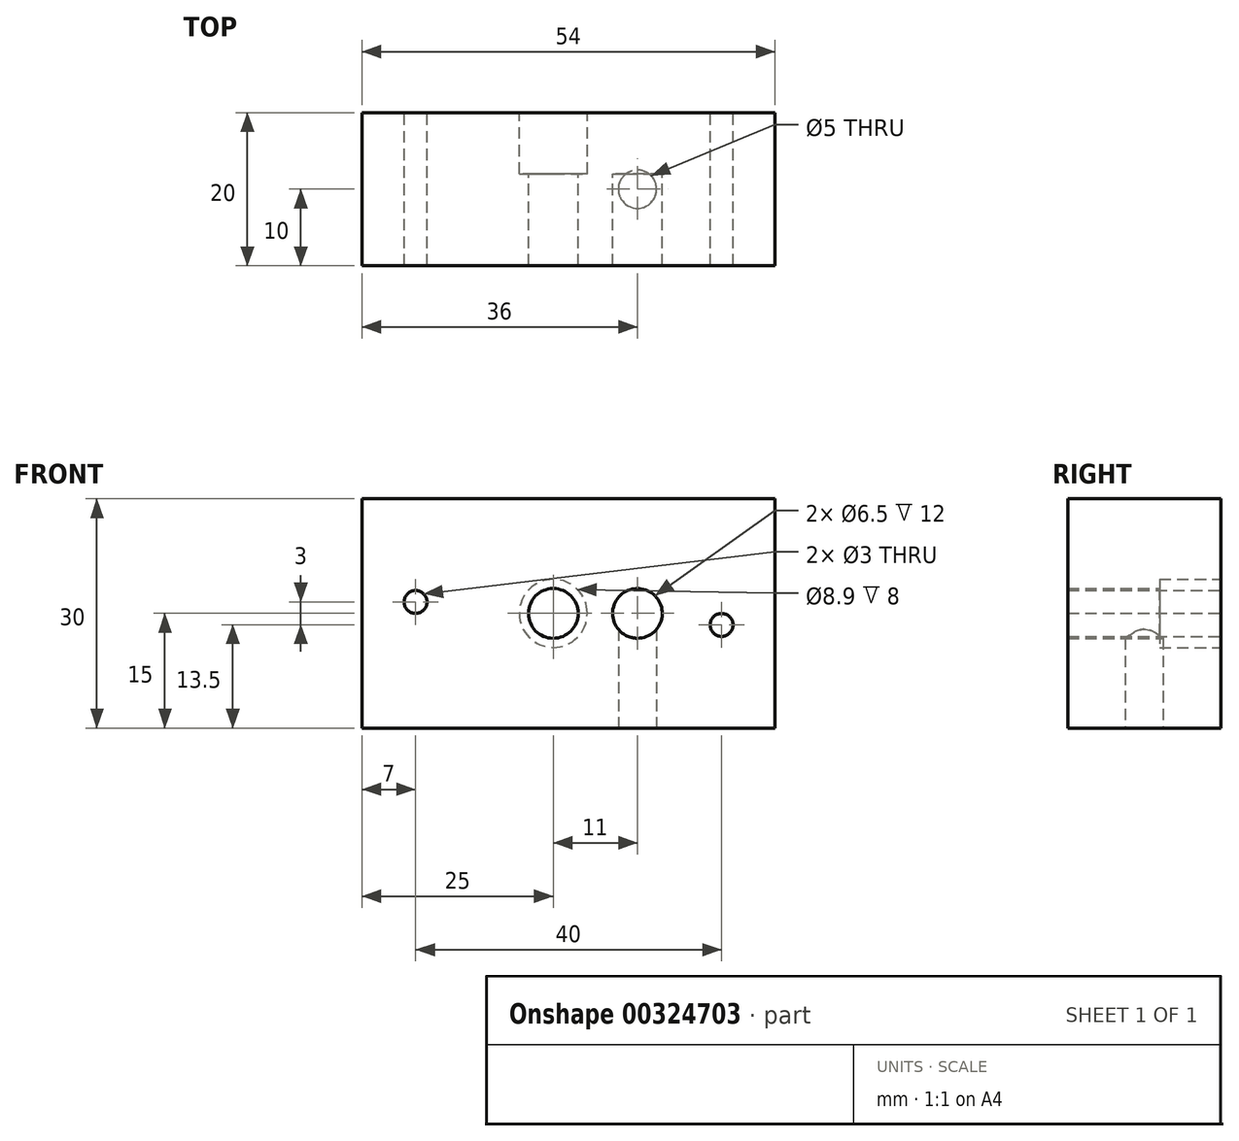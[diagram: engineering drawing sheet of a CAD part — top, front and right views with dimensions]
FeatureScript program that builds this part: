
annotation { "Feature Type Name" : "Feature", "Feature Type Description" : "" }
export const myFeature = defineFeature(function(context is Context, id is Id, definition is map)
    precondition{}
    {
        {
            var Q0;
            Q0=qCreatedBy(makeId("Front.planeOp"),FACE);
            var sketch = newSketch(context, id + "F0", { "sketchPlane" : qUnion([Q0])});
            skLineSegment(sketch, "E0.bottom", {"start": v(0, 0) * mm, "end": v(54, 0) * mm});
            skLineSegment(sketch, "E0.top", {"start": v(0, 30) * mm, "end": v(54, 30) * mm});
            skLineSegment(sketch, "E0.left", {"start": v(0, 0) * mm, "end": v(0, 30) * mm});
            skLineSegment(sketch, "E0.right", {"start": v(54, 0) * mm, "end": v(54, 30) * mm});
            skCircle(sketch, "E1", {"center": v(7, 16.5) * mm, "radius": 1.5 * mm});
            skCircle(sketch, "E2", {"center": v(25, 15) * mm, "radius": 3.25 * mm});
            skCircle(sketch, "E3", {"center": v(47, 13.5) * mm, "radius": 1.5 * mm});
            skCircle(sketch, "E4", {"center": v(36, 15) * mm, "radius": 3.25 * mm});
            skLineSegment(sketch, "E5", {"start": v(25, 15) * mm, "end": v(36, 15) * mm, "construction": true});
            skLineSegment(sketch, "E6", {"start": v(47, 15) * mm, "end": v(36, 15) * mm, "construction": true});
            skLineSegment(sketch, "E7", {"start": v(7, 15) * mm, "end": v(25, 15) * mm, "construction": true});
            skSolve(sketch);
        }
        {
            var Q0;
            Q0 = qSketchRegion(id + "F0", true);
            extrude(context, id + "F1", {"entities" : qUnion([Q0]), "depth" : 20 * mm});
        }
        {
            var Q0;
            Q0=makeQuery(id+"F1.opExtrude","CAP_FACE",FACE,{"disambiguationData":[OSD([sQuery(id+"F0.wireOp",EDGE,"E0.bottom"),sQuery(id+"F0.wireOp",EDGE,"E0.top"),sQuery(id+"F0.wireOp",EDGE,"E0.left"),sQuery(id+"F0.wireOp",EDGE,"E0.right"),sQuery(id+"F0.wireOp",EDGE,"E1"),sQuery(id+"F0.wireOp",EDGE,"E2"),sQuery(id+"F0.wireOp",EDGE,"E3"),sQuery(id+"F0.wireOp",EDGE,"E4")])],"isStart":false});
            var sketch = newSketch(context, id + "F2", { "sketchPlane" : qUnion([Q0])});
            skLineSegment(sketch, "E8.bottom", {"start": v(0, 0) * mm, "end": v(54, 0) * mm});
            skLineSegment(sketch, "E8.top", {"start": v(0, 30) * mm, "end": v(54, 30) * mm});
            skLineSegment(sketch, "E8.left", {"start": v(0, 0) * mm, "end": v(0, 30) * mm});
            skLineSegment(sketch, "E8.right", {"start": v(54, 0) * mm, "end": v(54, 30) * mm});
            skLineSegment(sketch, "E9.bottom", {"start": v(3.5, 3.5) * mm, "end": v(50.5, 3.5) * mm});
            skLineSegment(sketch, "E9.top", {"start": v(3.5, 26.5) * mm, "end": v(50.5, 26.5) * mm});
            skLineSegment(sketch, "E9.left", {"start": v(3.5, 3.5) * mm, "end": v(3.5, 26.5) * mm});
            skLineSegment(sketch, "E9.right", {"start": v(50.5, 3.5) * mm, "end": v(50.5, 26.5) * mm});
            skSolve(sketch);
        }
        {
            var Q0;
            Q0=makeQuery(id+"F1.opExtrude","SWEPT_FACE",FACE,{"disambiguationData":[OSD([sQuery(id+"F0.wireOp",EDGE,"E0.bottom")])]});
            var sketch = newSketch(context, id + "F3", { "sketchPlane" : qUnion([Q0])});
            skCircle(sketch, "E10", {"center": v(36, 10) * mm, "radius": 2.5 * mm});
            skSolve(sketch);
        }
        {
            var Q0;
            Q0 = qSketchRegion(id + "F3", true);
            extrude(context, id + "F4", {"entities" : qUnion([Q0]), "operationType" : NewBodyOperationType.REMOVE, "oppositeDirection" : true, "depth" : 16 * mm});
        }
        {
            var Q0;
            Q0=makeQuery(id+"F1.opExtrude","CAP_FACE",FACE,{"disambiguationData":[OSD([sQuery(id+"F0.wireOp",EDGE,"E0.bottom"),sQuery(id+"F0.wireOp",EDGE,"E0.top"),sQuery(id+"F0.wireOp",EDGE,"E0.left"),sQuery(id+"F0.wireOp",EDGE,"E0.right"),sQuery(id+"F0.wireOp",EDGE,"E1"),sQuery(id+"F0.wireOp",EDGE,"E2"),sQuery(id+"F0.wireOp",EDGE,"E3"),sQuery(id+"F0.wireOp",EDGE,"E4")])],"isStart":true});
            var sketch = newSketch(context, id + "F5", { "sketchPlane" : qUnion([Q0])});
            skCircle(sketch, "E11", {"center": v(-36, 15) * mm, "radius": 3.25 * mm});
            skSolve(sketch);
        }
        {
            var Q0;
            Q0=makeQuery(id+"FoY2zCmdkDL0ALK_1.boolean.opBoolean","MERGE",FACE,{"derivedFrom":[makeQuery(id+"F1.opExtrude","CAP_FACE",FACE,{"disambiguationData":[OSD([sQuery(id+"F0.wireOp",EDGE,"E0.bottom"),sQuery(id+"F0.wireOp",EDGE,"E0.top"),sQuery(id+"F0.wireOp",EDGE,"E0.left"),sQuery(id+"F0.wireOp",EDGE,"E0.right"),sQuery(id+"F0.wireOp",EDGE,"E1"),sQuery(id+"F0.wireOp",EDGE,"E2"),sQuery(id+"F0.wireOp",EDGE,"E3"),sQuery(id+"F0.wireOp",EDGE,"E4")])],"isStart":true}),makeQuery(id+"FoY2zCmdkDL0ALK_1.opExtrude","CAP_FACE",FACE,{"disambiguationData":[OSD([sQuery(id+"F5.wireOp",EDGE,"E11")])],"isStart":true})]});
            var sketch = newSketch(context, id + "F6", { "sketchPlane" : qUnion([Q0])});
            skCircle(sketch, "E12", {"center": v(-25, 15) * mm, "radius": 4.45 * mm});
            skSolve(sketch);
        }
        {
            var Q0;
            Q0 = qSketchRegion(id + "F6", true);
            extrude(context, id + "F7", {"entities" : qUnion([Q0]), "operationType" : NewBodyOperationType.REMOVE, "oppositeDirection" : true, "depth" : 8 * mm});
        }
        {
            var Q0;
            Q0 = qSketchRegion(id + "F5", true);
            extrude(context, id + "F8", {"entities" : qUnion([Q0]), "operationType" : NewBodyOperationType.ADD, "oppositeDirection" : true, "depth" : 8 * mm});
        }
    });
